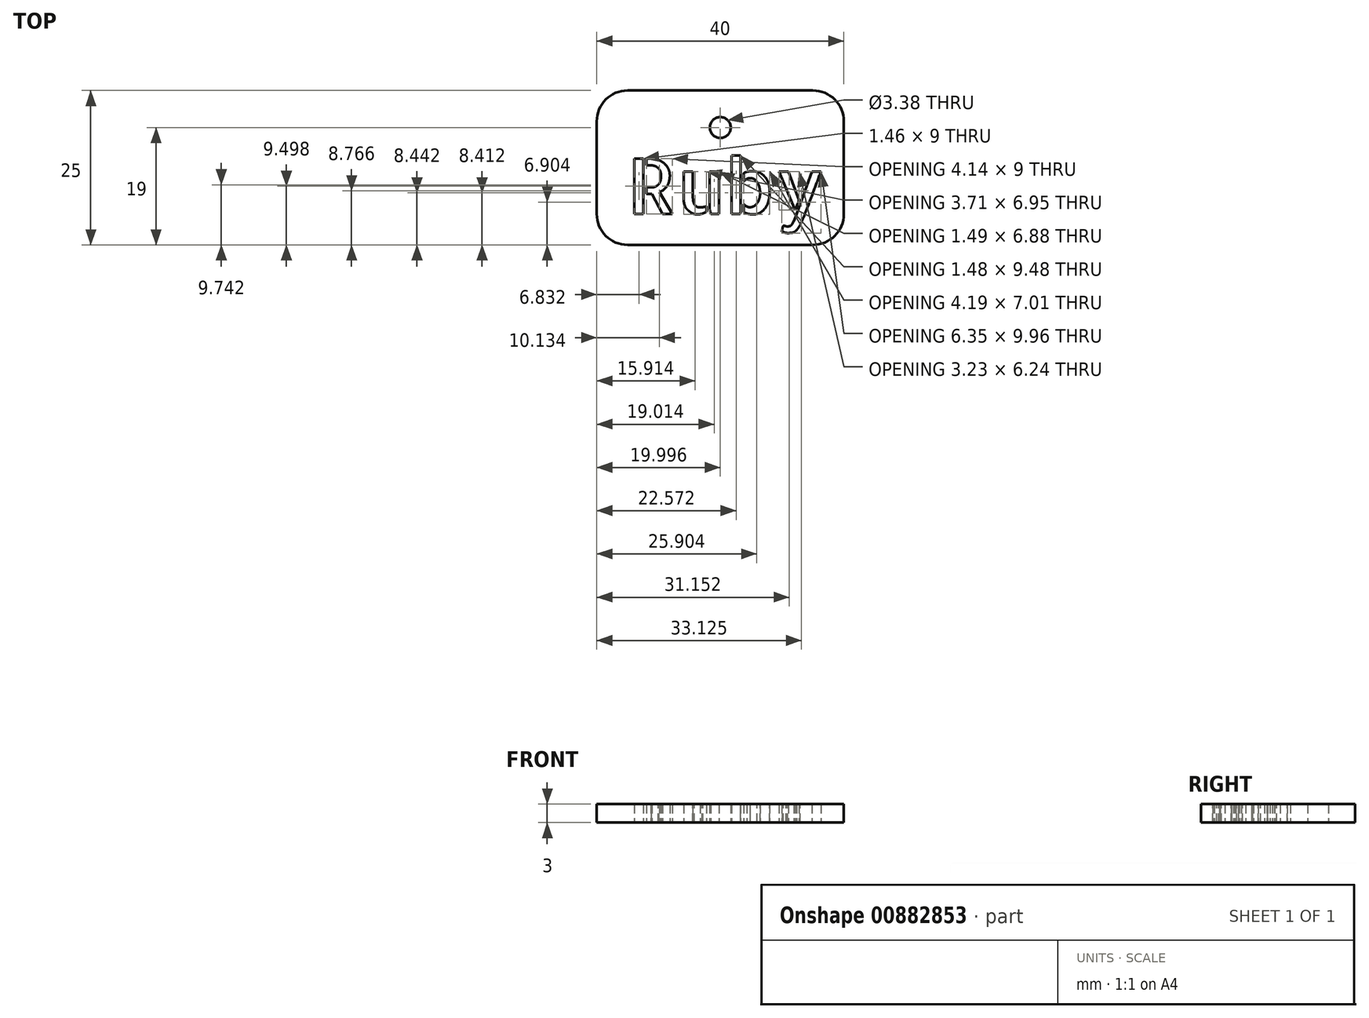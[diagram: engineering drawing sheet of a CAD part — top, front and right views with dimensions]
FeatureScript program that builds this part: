
annotation { "Feature Type Name" : "Feature", "Feature Type Description" : "" }
export const myFeature = defineFeature(function(context is Context, id is Id, definition is map)
    precondition{}
    {
        {
            var Q0;
            Q0=qCreatedBy(makeId("Top.planeOp"),FACE);
            var sketch = newSketch(context, id + "F0", { "sketchPlane" : qUnion([Q0])});
            skLineSegment(sketch, "E0.bottom", {"start": v(-9.6, 20) * mm, "end": v(20.4, 20) * mm});
            skLineSegment(sketch, "E0.top", {"start": v(-9.6, -5) * mm, "end": v(20.4, -5) * mm});
            skLineSegment(sketch, "E0.left", {"start": v(-14.6, 15) * mm, "end": v(-14.6, 0) * mm});
            skLineSegment(sketch, "E0.right", {"start": v(25.4, 15) * mm, "end": v(25.4, 0) * mm});
            skPoint(sketch, "E1.visualSharp", {"position": v(-14.6, 20) * mm});
            skArc(sketch, "E1.filletArc", {"start": v(-9.6, 20) * mm, "mid": v(-13.14, 18.54) * mm, "end": v(-14.6, 15) * mm});
            skPoint(sketch, "E2.visualSharp", {"position": v(25.4, 20) * mm});
            skArc(sketch, "E2.filletArc", {"start": v(25.4, 15) * mm, "mid": v(23.93, 18.54) * mm, "end": v(20.4, 20) * mm});
            skPoint(sketch, "E3.visualSharp", {"position": v(25.4, -5) * mm});
            skArc(sketch, "E3.filletArc", {"start": v(20.4, -5) * mm, "mid": v(23.93, -3.54) * mm, "end": v(25.4, 0) * mm});
            skPoint(sketch, "E4.visualSharp", {"position": v(-14.6, -5) * mm});
            skArc(sketch, "E4.filletArc", {"start": v(-14.6, 0) * mm, "mid": v(-13.14, -3.54) * mm, "end": v(-9.6, -5) * mm});
            skCircle(sketch, "E5", {"center": v(5.4, 14) * mm, "radius": 1.7 * mm});
            skText(sketch, "E6", { "text": "Ruby", "fontName": "AllertaStencil-Regular.ttf"});
            const initialGuessF0  = {"E6": [-0.0096, 0, 1, 0, 0.009]};
            skSetInitialGuess(sketch, initialGuessF0);
            skSolve(sketch);
        }
        {
            var Q0;
            Q0 = qSketchRegion(id + "F0", true);
            extrude(context, id + "F1", {"entities" : qUnion([Q0]), "depth" : 3 * mm, "offsetDistance" : 25 * mm});
        }
    });
